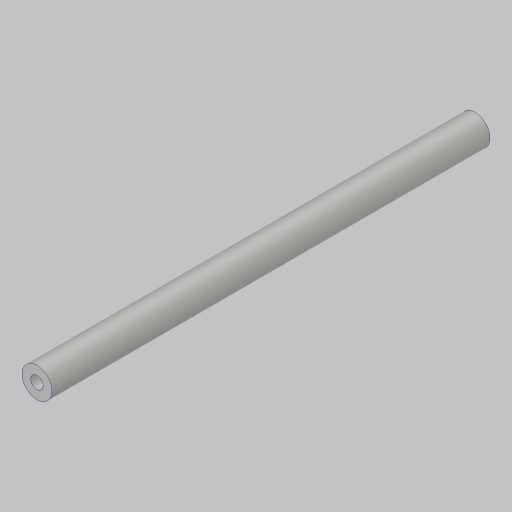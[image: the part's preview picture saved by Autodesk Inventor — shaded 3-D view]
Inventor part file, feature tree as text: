
AUTODESK INVENTOR PART (.ipt)
format: ipt  version: 2023.5 (Build 275446000, 446)  size: 98,816 bytes
history: native  units: in
note: dims shown in document units (in); Inventor stores cm internally (conversion verified against a paired STEP export)
features: extrude x1, hole x1
ambient origin geometry x8: Origin, YZ Plane, XZ Plane, XY Plane, X Axis, Y Axis, Z Axis, Center Point
bodies: Solid1 (feature_tree)
feature tree (2):
  extrude  "Extrusion1"  Depth=5.5in
  hole  "Hole1"  [1 undecoded]
note: 1 required parameter value undecoded (feature->parameter linkage not recoverable at this tier; creation-order binding heuristic only, values carry confidence <= 0.55)
